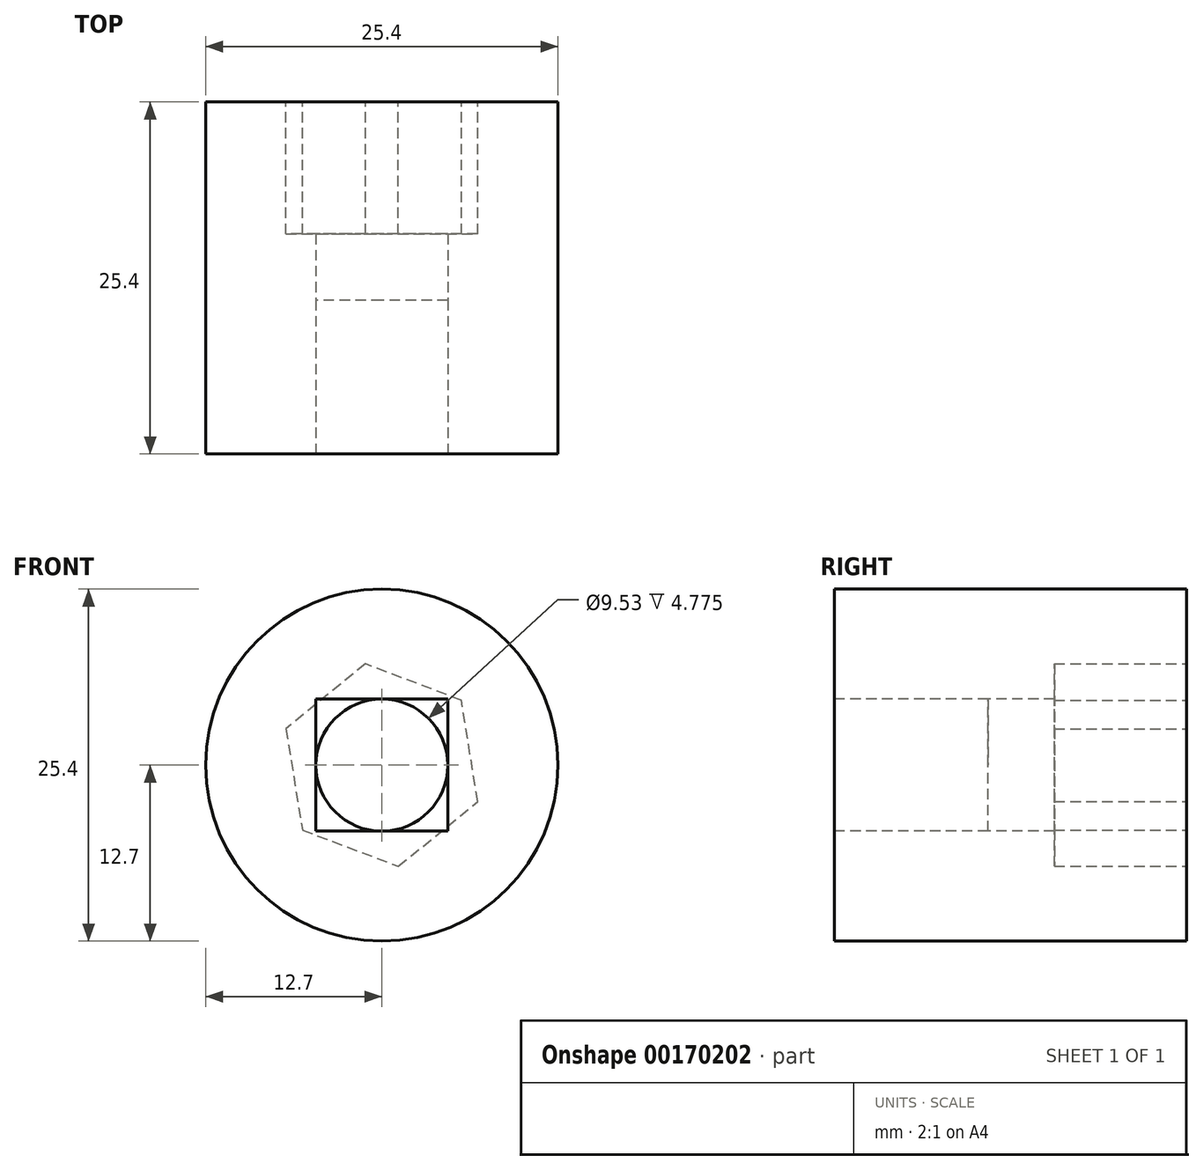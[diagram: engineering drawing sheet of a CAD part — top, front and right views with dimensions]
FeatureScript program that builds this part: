
annotation { "Feature Type Name" : "Feature", "Feature Type Description" : "" }
export const myFeature = defineFeature(function(context is Context, id is Id, definition is map)
    precondition{}
    {
        {
            var Q0;
            Q0=qCreatedBy(makeId("Front.planeOp"),FACE);
            var sketch = newSketch(context, id + "F0", { "sketchPlane" : qUnion([Q0])});
            skCircle(sketch, "E0", {"center": v(0, 0) * mm, "radius": 12.7 * mm});
            skSolve(sketch);
        }
        {
            var Q0;
            Q0=makeQuery(id+"F0.imprint","IMPRINT",FACE,{"disambiguationData":[TD([[makeQuery(id+"F0.imprint","IMPRINT",EDGE,{"derivedFrom":sQuery(id+"F0.wireOp",EDGE,"E0")}),1.0]])]});
            extrude(context, id + "F1", {"entities" : qUnion([Q0]), "oppositeDirection" : true, "depth" : 25.4 * mm});
        }
        {
            var Q0;
            Q0=qCreatedBy(makeId("Front.planeOp"),FACE);
            var sketch = newSketch(context, id + "F2", { "sketchPlane" : qUnion([Q0])});
            skLineSegment(sketch, "E1.bottom", {"start": v(4.76, -4.76) * mm, "end": v(-4.76, -4.76) * mm});
            skLineSegment(sketch, "E1.top", {"start": v(4.76, 4.76) * mm, "end": v(-4.76, 4.76) * mm});
            skLineSegment(sketch, "E1.left", {"start": v(4.76, -4.76) * mm, "end": v(4.76, 4.76) * mm});
            skLineSegment(sketch, "E1.right", {"start": v(-4.76, -4.76) * mm, "end": v(-4.76, 4.76) * mm});
            skPoint(sketch, "E1.middle", {"position": v(0, 0) * mm});
            skCircle(sketch, "E2", {"center": v(0, 0) * mm, "radius": 4.76 * mm});
            skSolve(sketch);
        }
        {
            var Q0;
            {var subQ0=sQuery(id+"F2.wireOp",EDGE,"E2");var subQ1=makeQuery(id+"F2.imprint","INTERSECT",VERTEX,{"derivedFrom":[sQuery(id+"F2.wireOp",EDGE,"E1.top"),subQ0]});Q0=makeQuery(id+"F2.imprint","IMPRINT",FACE,{"disambiguationData":[TD([[makeQuery(id+"F2.imprint","IMPRINT",EDGE,{"disambiguationData":[TD([[subQ1,1.0]])],"derivedFrom":subQ0}),1.0]])]});}
            extrude(context, id + "F3", {"entities" : qUnion([Q0]), "operationType" : NewBodyOperationType.REMOVE, "endBound" : BoundingType.THROUGH_ALL, "oppositeDirection" : true, "depth" : 25.4 * mm});
        }
        {
            var Q0;
            Q0 = qSketchRegion(id + "F2", true);
            extrude(context, id + "F4", {"entities" : qUnion([Q0]), "operationType" : NewBodyOperationType.REMOVE, "oppositeDirection" : true, "depth" : 11.1 * mm});
        }
        {
            var Q0;
            Q0=makeQuery(id+"F1.opExtrude","CAP_FACE",FACE,{"disambiguationData":[OSD([sQuery(id+"F0.wireOp",EDGE,"E0")])],"isStart":false});
            var sketch = newSketch(context, id + "F5", { "sketchPlane" : qUnion([Q0])});
            skCircle(sketch, "E3.cCircle", {"center": v(0, 0) * mm, "radius": 6.4 * mm, "construction": true});
            skLineSegment(sketch, "E3.0", {"start": v(-1.19, -7.3) * mm, "end": v(-6.92, -2.62) * mm});
            skLineSegment(sketch, "E3.1", {"start": v(-6.92, -2.62) * mm, "end": v(-5.73, 4.68) * mm});
            skLineSegment(sketch, "E3.2", {"start": v(-5.73, 4.68) * mm, "end": v(1.19, 7.3) * mm});
            skLineSegment(sketch, "E3.3", {"start": v(1.19, 7.3) * mm, "end": v(6.92, 2.62) * mm});
            skLineSegment(sketch, "E3.4", {"start": v(6.92, 2.62) * mm, "end": v(5.73, -4.68) * mm});
            skLineSegment(sketch, "E3.5", {"start": v(5.73, -4.68) * mm, "end": v(-1.19, -7.3) * mm});
            skPoint(sketch, "E3.0.midPoint", {"position": v(-4.05, -4.96) * mm});
            skSolve(sketch);
        }
        {
            var Q0;
            Q0=makeQuery(id+"F5.imprint","IMPRINT",FACE,{"disambiguationData":[TD([[makeQuery(id+"F5.imprint","IMPRINT",EDGE,{"derivedFrom":sQuery(id+"F5.wireOp",EDGE,"E3.0")}),-1.0]])]});
            extrude(context, id + "F6", {"entities" : qUnion([Q0]), "operationType" : NewBodyOperationType.REMOVE, "oppositeDirection" : true, "depth" : 9.52 * mm});
        }
    });
